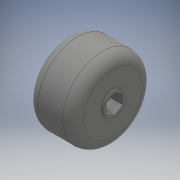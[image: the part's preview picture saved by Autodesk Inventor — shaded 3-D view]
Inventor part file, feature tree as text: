
AUTODESK INVENTOR PART (.ipt)
format: ipt  version: 2018.2 (Build 222227000, 227)  size: 176,640 bytes
history: native  units: mm
features: extrude x5, sketch x5, fillet x2, other x1, hole x1
ambient origin geometry x8: Origin, YZ Plane, XZ Plane, XY Plane, X Axis, Y Axis, Z Axis, Center Point
bodies: Body1 (feature_tree)
feature tree (14):
  other  "ソリッド1"
  extrude  "押し出し1"  Depth=38.1mm
  hole  "穴1"  [1 undecoded]
  extrude  "押し出し2"  Depth=10.0mm
  extrude  "押し出し3"  Depth=11.0mm
  fillet  "フィレット1"  Radius=0.7mm
  fillet  "フィレット2"  Radius=11.0mm
  sketch  "スケッチ4"
  sketch  "スケッチ5"
  extrude  "押し出し4"  Depth=0.7mm TaperAngle=0.0deg
  extrude  "押し出し5"  Depth=5.0mm
  sketch  "スケッチ1"
  sketch  "スケッチ2"
  sketch  "スケッチ3"
note: 1 required parameter value undecoded (feature->parameter linkage not recoverable at this tier; creation-order binding heuristic only, values carry confidence <= 0.55)
